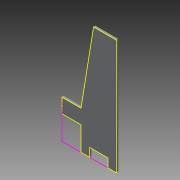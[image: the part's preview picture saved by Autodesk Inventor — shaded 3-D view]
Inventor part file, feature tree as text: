
AUTODESK INVENTOR PART (.ipt)
format: ipt  version: 2013 (Build 170138000, 138)  size: 107,520 bytes
history: native  units: mm
features: sketch x3, extrude x2
ambient origin geometry x8: Origin, YZ Plane, XZ Plane, XY Plane, X Axis, Y Axis, Z Axis, Center Point
bodies: Solid1 (feature_tree)
feature tree (5):
  extrude  "Extrusion1"  Depth=200.0mm
  sketch  "Sketch2"  dims[d6=20.0mm d7=0.0mm d8=370.0mm]
  sketch  "Sketch3"  dims[d9=150.0mm d10=250.0mm d11=90.0mm d12=90.0mm d13=190.0mm d14=240.0mm d16=10.0mm d17=0.0mm d18=8.0mm d19=1190.0mm]
  extrude  "Extrusion2"  Depth=370.0mm
  sketch  "Sketch1"  dims[d2=1200.0mm d4=200.0mm]
